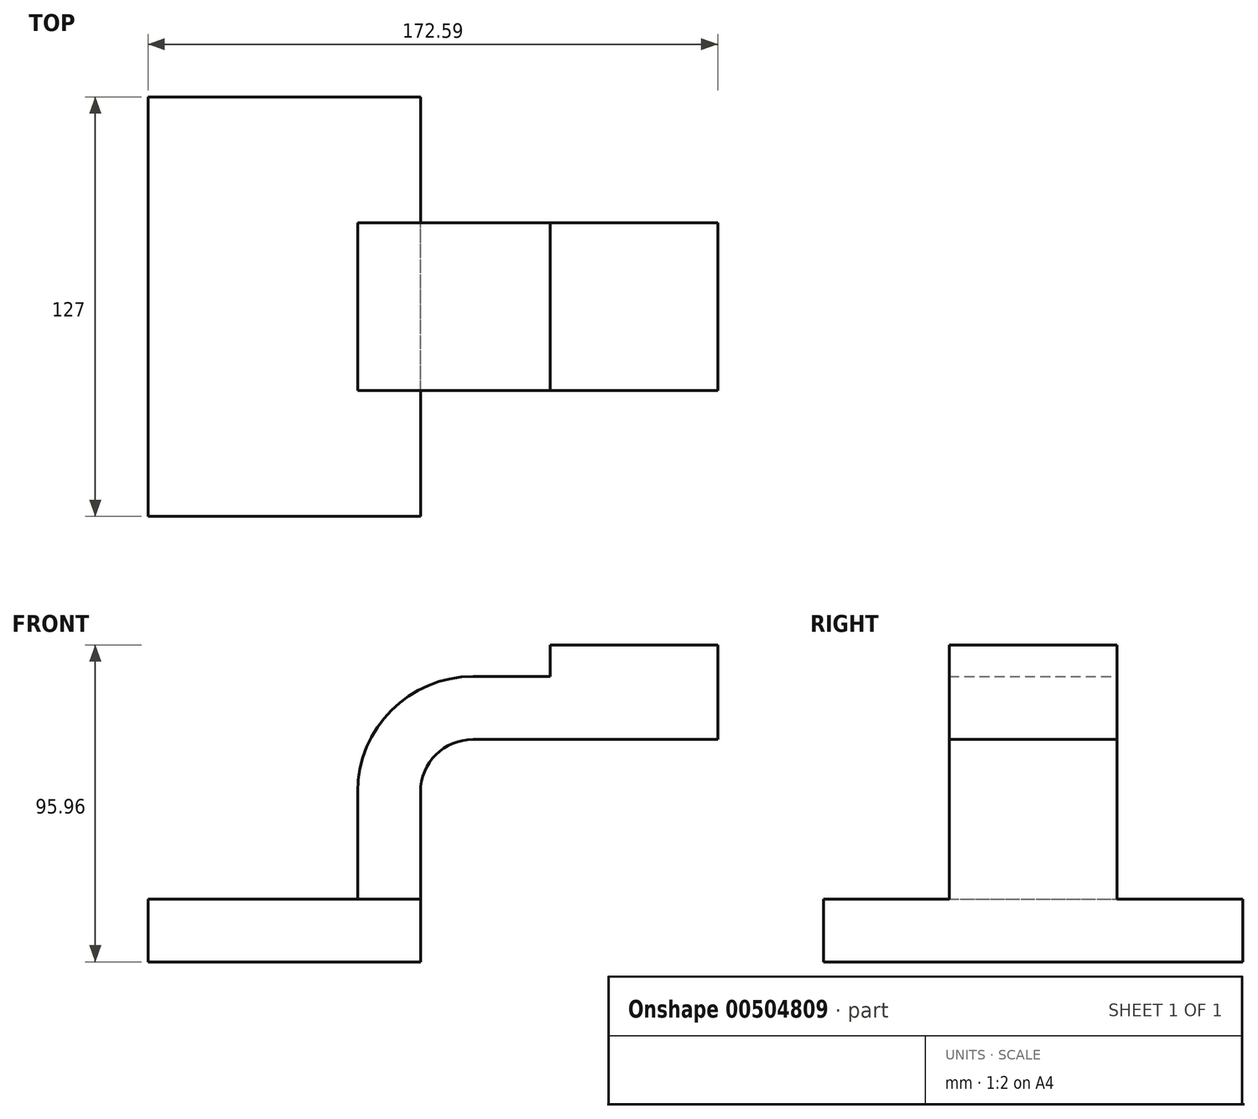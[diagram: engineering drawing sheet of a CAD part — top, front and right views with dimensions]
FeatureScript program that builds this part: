
annotation { "Feature Type Name" : "Feature", "Feature Type Description" : "" }
export const myFeature = defineFeature(function(context is Context, id is Id, definition is map)
    precondition{}
    {
        {
            var Q0;
            Q0=qCreatedBy(makeId("Front.planeOp"),FACE);
            var sketch = newSketch(context, id + "F0", { "sketchPlane" : qUnion([Q0])});
            skLineSegment(sketch, "E0.bottom", {"start": v(41.27, 9.53) * mm, "end": v(-41.28, 9.53) * mm});
            skLineSegment(sketch, "E0.top", {"start": v(41.28, -9.52) * mm, "end": v(-41.27, -9.53) * mm});
            skLineSegment(sketch, "E0.left", {"start": v(41.28, 9.53) * mm, "end": v(41.28, -9.52) * mm});
            skLineSegment(sketch, "E0.right", {"start": v(-41.28, 9.53) * mm, "end": v(-41.27, -9.53) * mm});
            skPoint(sketch, "E0.middle", {"position": v(0, 0) * mm});
            skLineSegment(sketch, "E1.bottom", {"start": v(80.5, 57.85) * mm, "end": v(131.3, 57.85) * mm});
            skLineSegment(sketch, "E1.top", {"start": v(80.5, 86.43) * mm, "end": v(131.3, 86.43) * mm});
            skLineSegment(sketch, "E1.left", {"start": v(80.5, 57.85) * mm, "end": v(80.5, 86.43) * mm});
            skLineSegment(sketch, "E1.right", {"start": v(131.3, 57.85) * mm, "end": v(131.3, 86.43) * mm});
            skPoint(sketch, "E1.middle", {"position": v(105.9, 72.14) * mm});
            skLineSegment(sketch, "E2.top", {"start": v(41.28, 17.21) * mm, "end": v(41.28, 17.21) * mm});
            skPoint(sketch, "E2.middle", {"position": v(41.27, 9.53) * mm});
            skLineSegment(sketch, "E3", {"start": v(41.27, 9.53) * mm, "end": v(41.27, 41.98) * mm});
            skArc(sketch, "E4", {"start": v(41.27, 41.98) * mm, "mid": v(45.92, 53.2) * mm, "end": v(57.15, 57.85) * mm});
            skLineSegment(sketch, "E5", {"start": v(57.15, 57.85) * mm, "end": v(80.5, 57.85) * mm});
            skLineSegment(sketch, "E6.0", {"start": v(57.15, 76.9) * mm, "end": v(80.55, 76.9) * mm});
            skArc(sketch, "E6.1", {"start": v(22.22, 41.98) * mm, "mid": v(32.45, 66.68) * mm, "end": v(57.15, 76.9) * mm});
            skLineSegment(sketch, "E6.2", {"start": v(22.23, 9.53) * mm, "end": v(22.23, 41.98) * mm});
            skFitSpline(sketch, "E7", {"points": [v(-41.28, 9.53) * mm, v(57.15, 76.9) * mm], "startDerivative": vector(-2.7, 102.4) * mm, "endDerivative": vector(113.4, -12.5) * mm});
            skSolve(sketch);
        }
        {
            var Q0;
            Q0=makeQuery(id+"F0.imprint","IMPRINT",FACE,{"disambiguationData":[TD([[makeQuery(id+"F0.imprint","IMPRINT",EDGE,{"derivedFrom":sQuery(id+"F0.wireOp",EDGE,"E0.top")}),-1.0]])]});
            extrude(context, id + "F1", {"entities" : qUnion([Q0]), "endBound" : BoundingType.SYMMETRIC, "depth" : 127 * mm});
        }
        {
            var Q0;
            {var subQ0=sQuery(id+"F0.wireOp",EDGE,"E3");Q0=makeQuery(id+"F0.imprint","IMPRINT",FACE,{"disambiguationData":[TD([[makeQuery(id+"F0.imprint","IMPRINT",EDGE,{"derivedFrom":subQ0}),1.0]])]});}
            extrude(context, id + "F2", {"entities" : qUnion([Q0]), "operationType" : NewBodyOperationType.ADD, "endBound" : BoundingType.SYMMETRIC, "depth" : 50.8 * mm});
        }
        {
            var Q0;
            {var subQ3=sQuery(id+"F0.wireOp",EDGE,"E1.bottom");Q0=makeQuery(id+"F0.imprint","IMPRINT",FACE,{"disambiguationData":[TD([[makeQuery(id+"F0.imprint","IMPRINT",EDGE,{"derivedFrom":subQ3}),1.0]])]});}
            extrude(context, id + "F3", {"entities" : qUnion([Q0]), "operationType" : NewBodyOperationType.ADD, "endBound" : BoundingType.SYMMETRIC, "depth" : 50.8 * mm});
        }
        {
            var Q0;
            Q0=makeQuery(id+"F0.imprint","IMPRINT",FACE,{"disambiguationData":[TD([[makeQuery(id+"F0.imprint","IMPRINT",EDGE,{"derivedFrom":sQuery(id+"F0.wireOp",EDGE,"E6.1")}),1.0]])]});
            extrude(context, id + "F4", {"entities" : qUnion([Q0]), "operationType" : NewBodyOperationType.ADD, "endBound" : BoundingType.SYMMETRIC, "depth" : 15.88 * mm});
        }
    });
